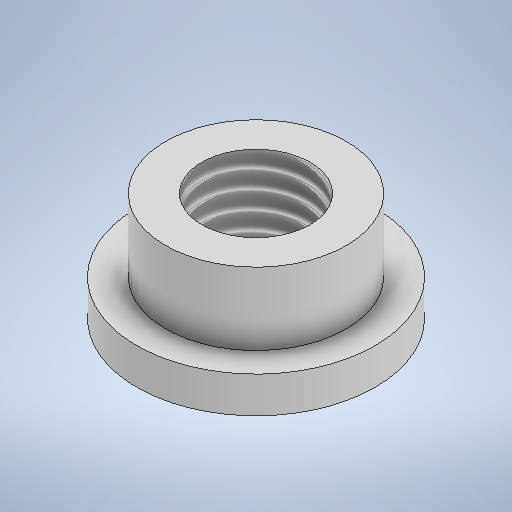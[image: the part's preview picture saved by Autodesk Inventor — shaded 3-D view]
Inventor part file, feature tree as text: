
AUTODESK INVENTOR PART (.ipt)
format: ipt  version: 2025.2 (Build 292293000, 293)  size: 264,192 bytes
history: native  units: mm
features: sketch x4, extrude x3, thread x1
ambient origin geometry x8: Origin, YZ Plane, XZ Plane, XY Plane, X Axis, Y Axis, Z Axis, Center Point
bodies: Solid1 (feature_tree)
feature tree (8):
  extrude  "Extrusion1"  Depth=1.0mm TaperAngle=0.0deg
  sketch  "Sketch2"  dims[d3=5.0mm d4=2.0mm d5=0.0mm]
  extrude  "Extrusion2"  Depth=2.0mm TaperAngle=0.0deg
  extrude  "Extrusion3"  Depth=3.0mm TaperAngle=0.0deg
  thread  "Thread1"  [1 undecoded]
  sketch  "Sketch1"  dims[d0=6.6mm d1=1.0mm d2=0.0mm]
  sketch  "Sketch3"  dims[d6=3.0mm d7=3.0mm d8=0.0mm d9=3.0mm d10=0.0mm]
  sketch  "Sketch4"
note: 1 required parameter value undecoded (feature->parameter linkage not recoverable at this tier; creation-order binding heuristic only, values carry confidence <= 0.55)
